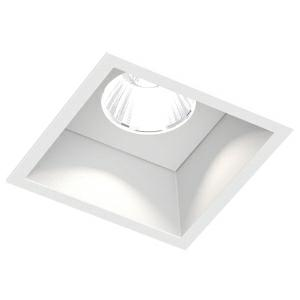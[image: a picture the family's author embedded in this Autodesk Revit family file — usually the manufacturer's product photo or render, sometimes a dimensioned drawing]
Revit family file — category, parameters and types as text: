
# Revit family: 4di_220-0373
name_source: partatom
category: Lighting Fixtures
units: mm (PartAtom-declared; Revit-internal decimal feet)

## family parameters
Cut with Voids When Loaded = No
Host = Face
Light Source = No
Part Type = Normal
Room Calculation Point = No
Round Connector Dimension = Use Diameter
Shared = No

## types (1)
- 220-0373-K20 (1 x LED, 1182 lm, 13 W, Natural Dim)
    Apparent Load = 13 VA
    Approval mark = CE
    CIE Flux Codes = 99 100 100 100 67
    Color Rendering = 1A/90…99
    Color Temperature = Natural Dim
    Default Elevation = 1800 mm
    Description = 4DI
    Height = 0 mm  [stored 0 ft]
    Lamp = 1 x LED
    Lamp Light Flux = 1182 lm
    Lamp Power = 13 W
    Lamp count = 1
    Length = 92 mm
    Luminous efficacy = 61 lm/W
    Manufacturer = Prolicht
    ModVariant = No
    Model = 220-0373
    Mounting Place = Ceiling
    Mounting Type = Recessed
    Number of Poles = 1
    OnlyDefault = Yes
    Power Factor = 1
    Product Name = 4DI
    Product group = Recessed spotlights
    ProductGroupID = 422
    Protection Class = Safety extra-low voltage
    Protection Degree = IP 20
    RLX_Detail_Level = 1
    RLX_Emergency_Light_Flux = 0 lm
    RLX_Emergency_Type = 0
    RLX_Emergency_Type_DB = No
    RlxData = <blob elided: 307049 chars, md5=55cf5dc5>
    Socket = socket
    Standby Power = 0 W
    System Light Flux = 792 lm
    System Power = 13 W
    Type Comments = REFLECTOR 20° (20)
    Type Image = 220-0373.jpg
    URL = http://relux.com
    VarID = 220-0373-k20
    Voltage = 0 V
    Weight = 0.00 kg
    Width = 92 mm

note: [stored X ft] marks values corroborated as IEEE doubles in the binary element streams (Revit-internal decimal feet)

## geometry (parser evidence)
native form markers: Blend x4, Sweep x12
no freeform markers — native parametric forms only
